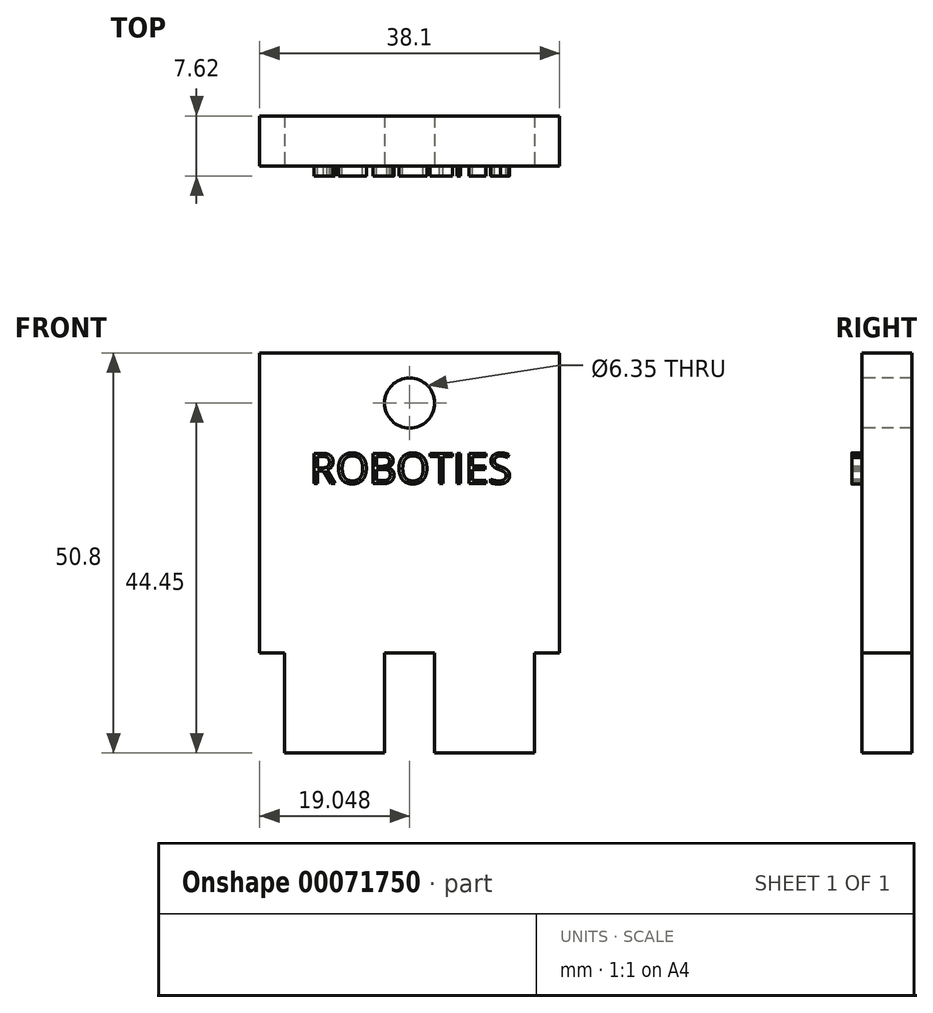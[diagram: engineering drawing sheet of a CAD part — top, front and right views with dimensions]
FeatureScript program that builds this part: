
annotation { "Feature Type Name" : "Feature", "Feature Type Description" : "" }
export const myFeature = defineFeature(function(context is Context, id is Id, definition is map)
    precondition{}
    {
        {
            var Q0;
            Q0=qCreatedBy(makeId("Front.planeOp"),FACE);
            var sketch = newSketch(context, id + "F0", { "sketchPlane" : qUnion([Q0])});
            skLineSegment(sketch, "E0.bottom", {"start": v(-31.75, -58.77) * mm, "end": v(6.35, -58.77) * mm});
            skLineSegment(sketch, "E0.top", {"start": v(-31.75, -7.97) * mm, "end": v(6.35, -7.97) * mm});
            skLineSegment(sketch, "E0.left", {"start": v(-31.75, -58.77) * mm, "end": v(-31.75, -7.97) * mm});
            skLineSegment(sketch, "E0.right", {"start": v(6.35, -58.77) * mm, "end": v(6.35, -7.97) * mm});
            skSolve(sketch);
        }
        {
            var Q0;
            Q0 = qSketchRegion(id + "F0", true);
            extrude(context, id + "F1", {"entities" : qUnion([Q0]), "depth" : 6.35 * mm});
        }
        {
            var Q0;
            Q0=makeQuery(id+"F1.opExtrude","CAP_FACE",FACE,{"disambiguationData":[OSD([sQuery(id+"F0.wireOp",EDGE,"E0.bottom"),sQuery(id+"F0.wireOp",EDGE,"E0.top"),sQuery(id+"F0.wireOp",EDGE,"E0.left"),sQuery(id+"F0.wireOp",EDGE,"E0.right")])],"isStart":false});
            var sketch = newSketch(context, id + "F2", { "sketchPlane" : qUnion([Q0])});
            skLineSegment(sketch, "E1", {"start": v(-12.7, -58.77) * mm, "end": v(-12.7, -7.97) * mm, "construction": true});
            skLineSegment(sketch, "E2", {"start": v(-31.75, -14.32) * mm, "end": v(6.35, -14.32) * mm, "construction": true});
            skCircle(sketch, "E3", {"center": v(-12.7, -14.32) * mm, "radius": 3.18 * mm});
            skSolve(sketch);
        }
        {
            var Q0;
            Q0 = qSketchRegion(id + "F2", true);
            extrude(context, id + "F3", {"entities" : qUnion([Q0]), "operationType" : NewBodyOperationType.REMOVE, "endBound" : BoundingType.THROUGH_ALL, "oppositeDirection" : true, "depth" : 6.35 * mm});
        }
        {
            var Q0;
            Q0=makeQuery(id+"F1.opExtrude","CAP_FACE",FACE,{"disambiguationData":[OSD([sQuery(id+"F0.wireOp",EDGE,"E0.bottom"),sQuery(id+"F0.wireOp",EDGE,"E0.top"),sQuery(id+"F0.wireOp",EDGE,"E0.left"),sQuery(id+"F0.wireOp",EDGE,"E0.right")])],"isStart":false});
            var sketch = newSketch(context, id + "F4", { "sketchPlane" : qUnion([Q0])});
            skLineSegment(sketch, "E4.bottom", {"start": v(-28.58, -58.77) * mm, "end": v(-31.75, -58.77) * mm});
            skLineSegment(sketch, "E4.top", {"start": v(-28.58, -46.07) * mm, "end": v(-31.75, -46.07) * mm});
            skLineSegment(sketch, "E4.left", {"start": v(-28.58, -58.77) * mm, "end": v(-28.58, -46.07) * mm});
            skLineSegment(sketch, "E4.right", {"start": v(-31.75, -58.77) * mm, "end": v(-31.75, -46.07) * mm});
            skLineSegment(sketch, "E5.bottom", {"start": v(3.17, -58.77) * mm, "end": v(6.35, -58.77) * mm});
            skLineSegment(sketch, "E5.top", {"start": v(3.17, -46.07) * mm, "end": v(6.35, -46.07) * mm});
            skLineSegment(sketch, "E5.left", {"start": v(3.17, -58.77) * mm, "end": v(3.17, -46.07) * mm});
            skLineSegment(sketch, "E5.right", {"start": v(6.35, -58.77) * mm, "end": v(6.35, -46.07) * mm});
            skSolve(sketch);
        }
        {
            var Q0;
            Q0 = qSketchRegion(id + "F4", true);
            extrude(context, id + "F5", {"entities" : qUnion([Q0]), "operationType" : NewBodyOperationType.REMOVE, "endBound" : BoundingType.THROUGH_ALL, "oppositeDirection" : true, "depth" : 25.4 * mm});
        }
        {
            var Q0;
            Q0=makeQuery(id+"F1.opExtrude","CAP_FACE",FACE,{"disambiguationData":[OSD([sQuery(id+"F0.wireOp",EDGE,"E0.bottom"),sQuery(id+"F0.wireOp",EDGE,"E0.top"),sQuery(id+"F0.wireOp",EDGE,"E0.left"),sQuery(id+"F0.wireOp",EDGE,"E0.right")])],"isStart":false});
            var sketch = newSketch(context, id + "F6", { "sketchPlane" : qUnion([Q0])});
            skLineSegment(sketch, "E6.bottom", {"start": v(-15.88, -58.77) * mm, "end": v(-9.53, -58.77) * mm});
            skLineSegment(sketch, "E6.top", {"start": v(-15.88, -46.07) * mm, "end": v(-9.53, -46.07) * mm});
            skLineSegment(sketch, "E6.left", {"start": v(-15.88, -58.77) * mm, "end": v(-15.88, -46.07) * mm});
            skLineSegment(sketch, "E6.right", {"start": v(-9.53, -58.77) * mm, "end": v(-9.53, -46.07) * mm});
            skSolve(sketch);
        }
        {
            var Q0;
            Q0 = qSketchRegion(id + "F6", true);
            extrude(context, id + "F7", {"entities" : qUnion([Q0]), "operationType" : NewBodyOperationType.REMOVE, "endBound" : BoundingType.THROUGH_ALL, "oppositeDirection" : true, "depth" : 25.4 * mm});
        }
        {
            var Q0;
            Q0=makeQuery(id+"F1.opExtrude","CAP_FACE",FACE,{"disambiguationData":[OSD([sQuery(id+"F0.wireOp",EDGE,"E0.bottom"),sQuery(id+"F0.wireOp",EDGE,"E0.top"),sQuery(id+"F0.wireOp",EDGE,"E0.left"),sQuery(id+"F0.wireOp",EDGE,"E0.right")])],"isStart":false});
            var sketch = newSketch(context, id + "F8", { "sketchPlane" : qUnion([Q0])});
            skText(sketch, "E7", { "text": "ROBOTIES", "fontName": "OpenSans-Regular.ttf"});
            const initialGuessF8  = {"E7": [-0.0254, -0.02455, 1, 0, 0.00388]};
            skSetInitialGuess(sketch, initialGuessF8);
            skSolve(sketch);
        }
        {
            var Q0;
            Q0 = qSketchRegion(id + "F8", true);
            extrude(context, id + "F9", {"entities" : qUnion([Q0]), "operationType" : NewBodyOperationType.ADD, "depth" : 1.27 * mm});
        }
    });
